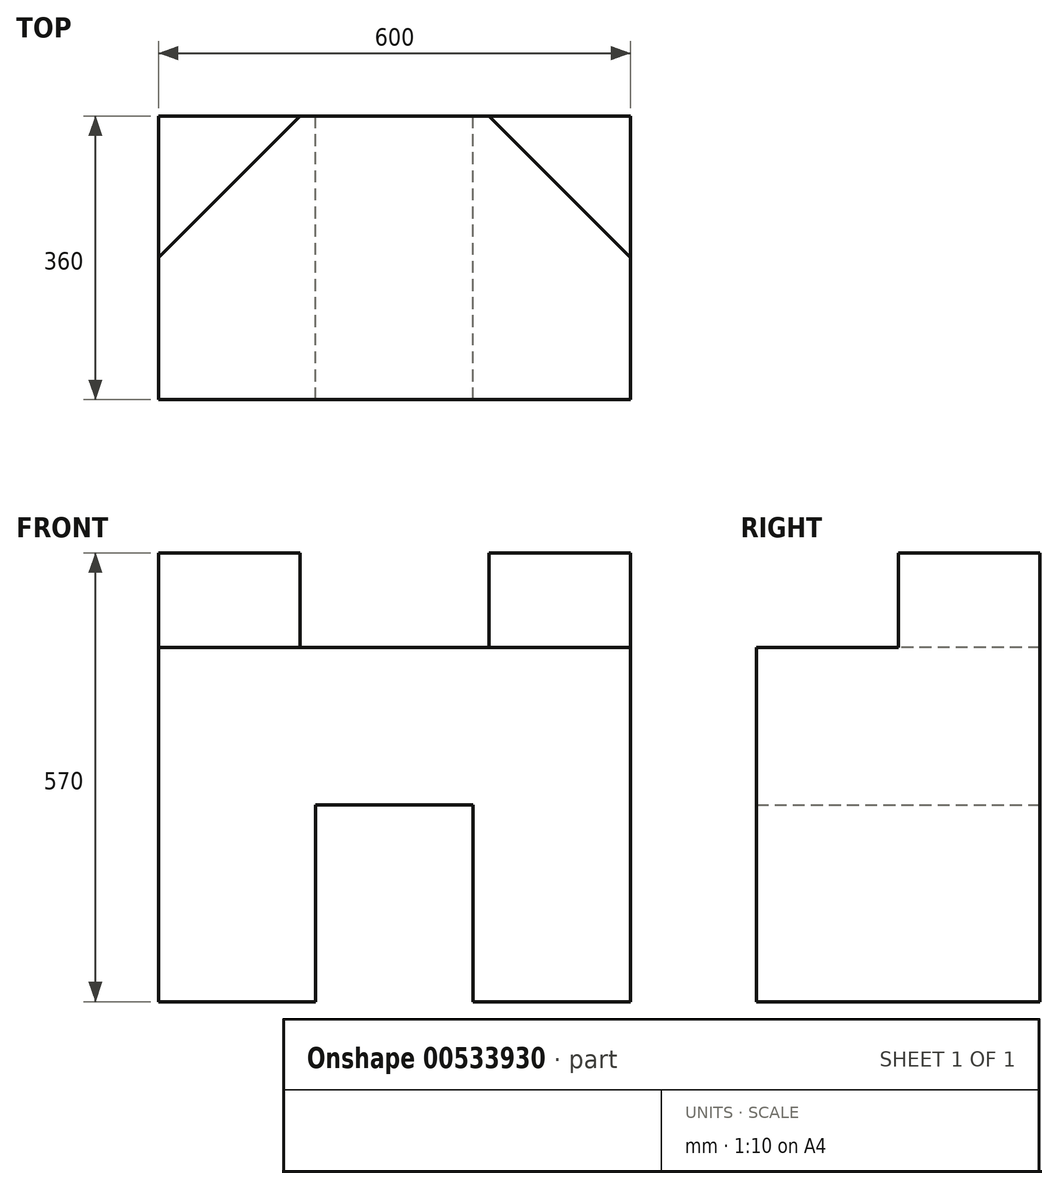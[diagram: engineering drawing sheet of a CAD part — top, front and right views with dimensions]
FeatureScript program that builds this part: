
annotation { "Feature Type Name" : "Feature", "Feature Type Description" : "" }
export const myFeature = defineFeature(function(context is Context, id is Id, definition is map)
    precondition{}
    {
        {
            var Q0;
            Q0=qCreatedBy(makeId("Front.planeOp"),FACE);
            var sketch = newSketch(context, id + "F0", { "sketchPlane" : qUnion([Q0])});
            skLineSegment(sketch, "E0.bottom", {"start": v(300, 225) * mm, "end": v(-300, 225) * mm});
            skLineSegment(sketch, "E0.top", {"start": v(300, -225) * mm, "end": v(-300, -225) * mm});
            skLineSegment(sketch, "E0.left", {"start": v(300, 225) * mm, "end": v(300, -225) * mm});
            skLineSegment(sketch, "E0.right", {"start": v(-300, 225) * mm, "end": v(-300, -225) * mm});
            skPoint(sketch, "E0.middle", {"position": v(0, 0) * mm});
            skLineSegment(sketch, "E1", {"start": v(-300, -225) * mm, "end": v(-100, -225) * mm});
            skLineSegment(sketch, "E2", {"start": v(-100, -225) * mm, "end": v(-100, 25) * mm});
            skLineSegment(sketch, "E3", {"start": v(-100, 25) * mm, "end": v(100, 25) * mm});
            skLineSegment(sketch, "E4", {"start": v(100, 25) * mm, "end": v(100, -225) * mm});
            skLineSegment(sketch, "E5", {"start": v(100, -225) * mm, "end": v(300, -225) * mm});
            skSolve(sketch);
        }
        {
            var Q0;
            Q0=makeQuery(id+"F0.imprint","IMPRINT",FACE,{"disambiguationData":[TD([[makeQuery(id+"F0.imprint","IMPRINT",EDGE,{"derivedFrom":sQuery(id+"F0.wireOp",EDGE,"E0.bottom")}),1.0]])]});
            extrude(context, id + "F1", {"entities" : qUnion([Q0]), "endBound" : BoundingType.SYMMETRIC, "depth" : 360 * mm, "offsetDistance" : 25 * mm});
        }
        {
            var Q0;
            Q0=makeQuery(id+"F1.opExtrude","SWEPT_FACE",FACE,{"disambiguationData":[OSD([sQuery(id+"F0.wireOp",EDGE,"E0.bottom")])]});
            var sketch = newSketch(context, id + "F2", { "sketchPlane" : qUnion([Q0])});
            skLineSegment(sketch, "E6", {"start": v(-300, 180) * mm, "end": v(-120, 180) * mm});
            skLineSegment(sketch, "E7", {"start": v(-120, 180) * mm, "end": v(-300, 0) * mm});
            skLineSegment(sketch, "E8", {"start": v(-300, 0) * mm, "end": v(-300, 180) * mm});
            skLineSegment(sketch, "E9", {"start": v(300, 180) * mm, "end": v(120, 180) * mm});
            skLineSegment(sketch, "E10", {"start": v(120, 180) * mm, "end": v(300, 0) * mm});
            skLineSegment(sketch, "E11", {"start": v(300, 0) * mm, "end": v(300, 180) * mm});
            skSolve(sketch);
        }
        {
            var Q0;
            Q0 = qSketchRegion(id + "F2", true);
            extrude(context, id + "F3", {"entities" : qUnion([Q0]), "operationType" : NewBodyOperationType.ADD, "depth" : 120 * mm, "offsetDistance" : 25 * mm});
        }
    });
